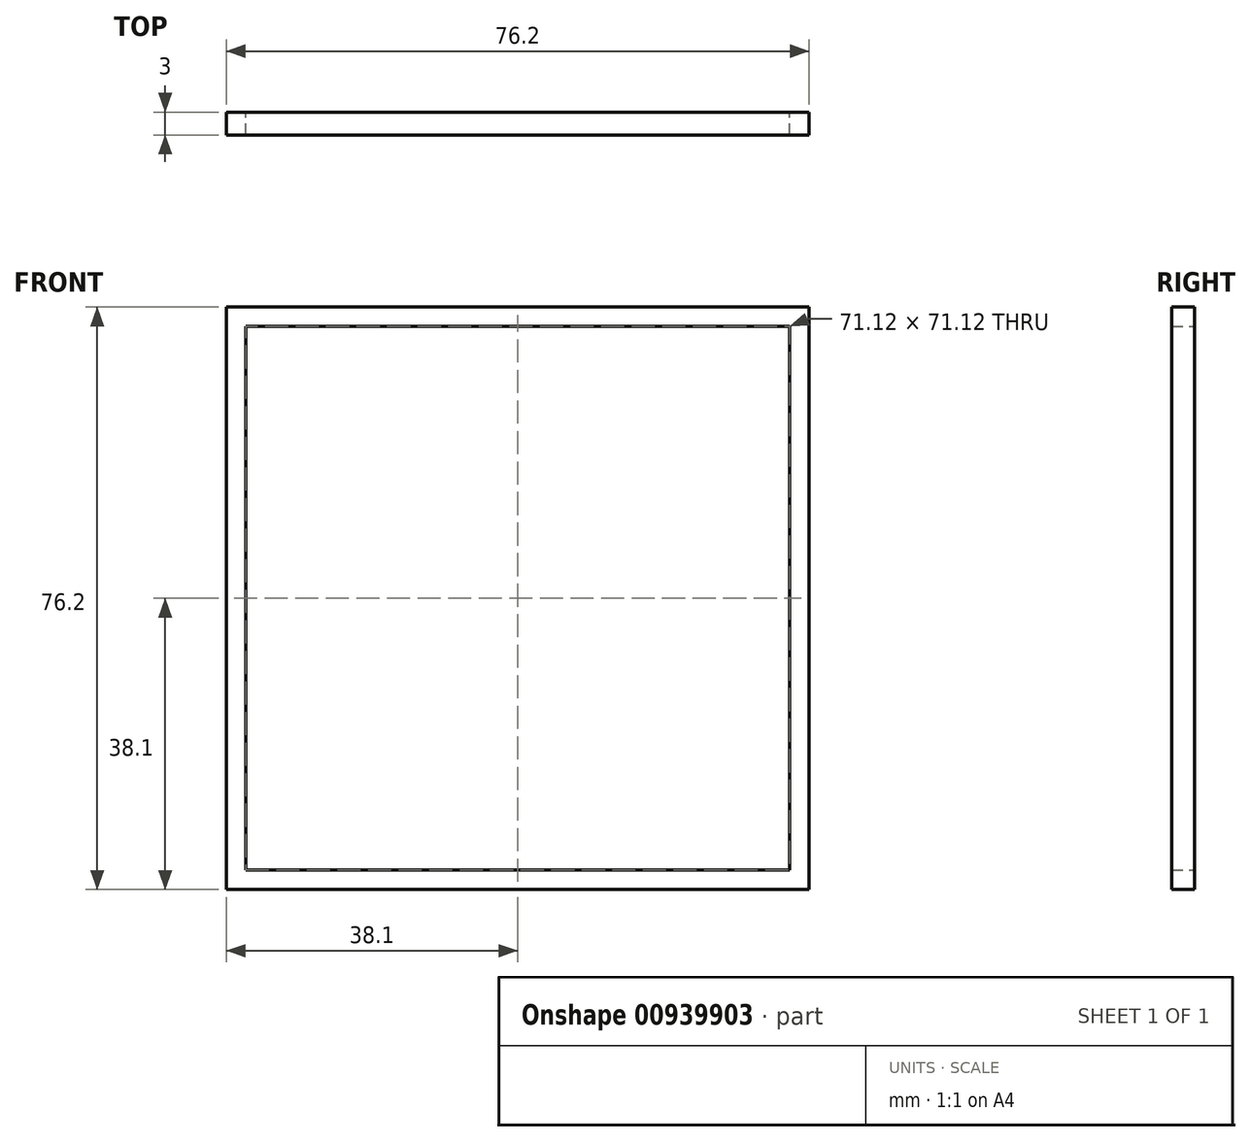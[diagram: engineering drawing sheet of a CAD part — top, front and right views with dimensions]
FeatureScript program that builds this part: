
annotation { "Feature Type Name" : "Feature", "Feature Type Description" : "" }
export const myFeature = defineFeature(function(context is Context, id is Id, definition is map)
    precondition{}
    {
        {
            assignVariable(context, id + "F0", {"name" : "size", "anyValue" : 3});
        }
        {
            var Q0;
            Q0=qCreatedBy(makeId("Front.planeOp"),FACE);
            var sketch = newSketch(context, id + "F1", { "sketchPlane" : qUnion([Q0])});
            skLineSegment(sketch, "E0.bottom", {"start": v(38.1, 38.1) * mm, "end": v(-38.1, 38.1) * mm});
            skLineSegment(sketch, "E0.top", {"start": v(38.1, -38.1) * mm, "end": v(-38.1, -38.1) * mm});
            skLineSegment(sketch, "E0.left", {"start": v(38.1, 38.1) * mm, "end": v(38.1, -38.1) * mm});
            skLineSegment(sketch, "E0.right", {"start": v(-38.1, 38.1) * mm, "end": v(-38.1, -38.1) * mm});
            skPoint(sketch, "E0.middle", {"position": v(0, 0) * mm});
            skSolve(sketch);
        }
        {
            var Q0;
            Q0=qSketchRegion(id+"F1",true);
            extrude(context, id + "F2", {"entities" : qUnion([Q0]), "depth" : (getVariable(context, 'size')) * mm, "offsetDistance" : 25.4 * mm});
        }
        {
            var Q0;
            Q0=makeQuery(id+"F2.opExtrude","CAP_FACE",FACE,{"disambiguationData":[OSD([sQuery(id+"F1.wireOp",EDGE,"E0.bottom"),sQuery(id+"F1.wireOp",EDGE,"E0.top"),sQuery(id+"F1.wireOp",EDGE,"E0.left"),sQuery(id+"F1.wireOp",EDGE,"E0.right")])],"isStart":false});
            var Q1;
            Q1=makeQuery(id+"F2.opExtrude","CAP_FACE",FACE,{"disambiguationData":[OSD([sQuery(id+"F1.wireOp",EDGE,"E0.bottom"),sQuery(id+"F1.wireOp",EDGE,"E0.top"),sQuery(id+"F1.wireOp",EDGE,"E0.left"),sQuery(id+"F1.wireOp",EDGE,"E0.right")])],"isStart":true});
            shell(context, id + "F3", {"entities" : qUnion([Q0, Q1]), "thickness" : 2.54 * mm});
        }
    });
